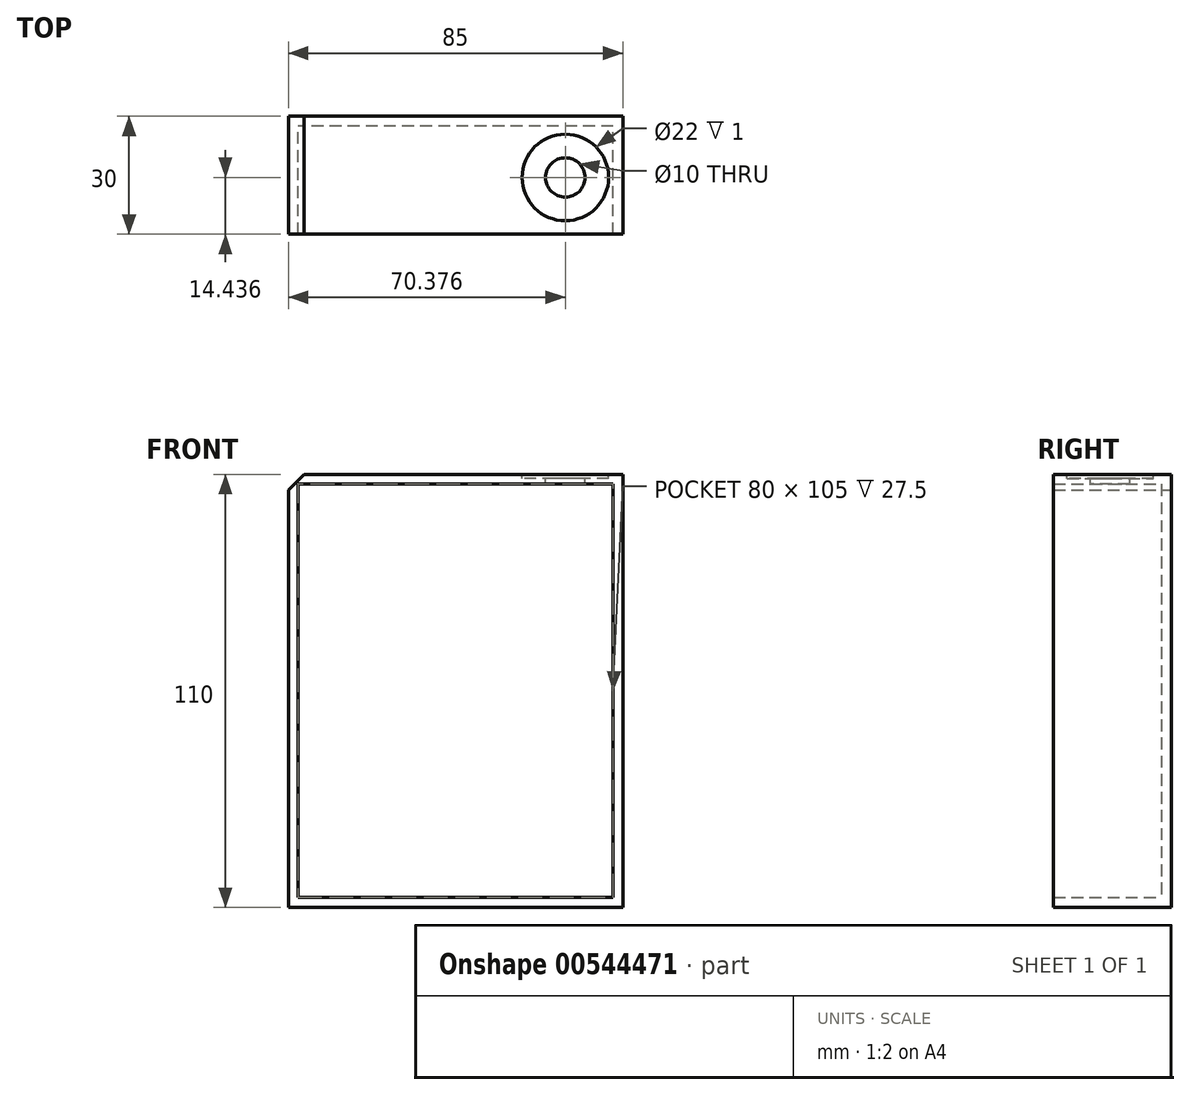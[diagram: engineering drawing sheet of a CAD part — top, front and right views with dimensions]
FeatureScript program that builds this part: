
annotation { "Feature Type Name" : "Feature", "Feature Type Description" : "" }
export const myFeature = defineFeature(function(context is Context, id is Id, definition is map)
    precondition{}
    {
        {
            var Q0;
            Q0=qCreatedBy(makeId("Front.planeOp"),FACE);
            var sketch = newSketch(context, id + "F0", { "sketchPlane" : qUnion([Q0])});
            skLineSegment(sketch, "E0.bottom", {"start": v(42.5, 55) * mm, "end": v(-42.5, 55) * mm});
            skLineSegment(sketch, "E0.top", {"start": v(42.5, -55) * mm, "end": v(-42.5, -55) * mm});
            skLineSegment(sketch, "E0.left", {"start": v(42.5, 55) * mm, "end": v(42.5, -55) * mm});
            skLineSegment(sketch, "E0.right", {"start": v(-42.5, 55) * mm, "end": v(-42.5, -55) * mm});
            skPoint(sketch, "E0.middle", {"position": v(0, 0) * mm});
            skLineSegment(sketch, "E1", {"start": v(-42.5, 37.63) * mm, "end": v(-24.86, 55) * mm});
            skSolve(sketch);
        }
        {
            var Q0;
            Q0 = qSketchRegion(id + "F0", true);
            extrude(context, id + "F1", {"entities" : qUnion([Q0]), "depth" : 30 * mm, "offsetDistance" : 25 * mm});
        }
        {
            var Q0;
            Q0=makeQuery(id+"F1.opExtrude","SWEPT_FACE",FACE,{"disambiguationData":[OSD([sQuery(id+"F0.wireOp",EDGE,"E0.bottom")])]});
            var sketch = newSketch(context, id + "F2", { "sketchPlane" : qUnion([Q0])});
            skCircle(sketch, "E2", {"center": v(25.32, -14.4) * mm, "radius": 11 * mm});
            skSolve(sketch);
        }
        {
            var Q0;
            Q0=makeQuery(id+"F2.imprint","IMPRINT",FACE,{"disambiguationData":[TD([[makeQuery(id+"F2.imprint","IMPRINT",EDGE,{"derivedFrom":sQuery(id+"F2.wireOp",EDGE,"E2")}),1.0]])]});
            extrude(context, id + "F3", {"entities" : qUnion([Q0]), "operationType" : NewBodyOperationType.ADD, "depth" : -0.5 * mm, "offsetDistance" : 25 * mm});
        }
        {
            var Q0;
            Q0=makeQuery(id+"F1.opExtrude","CAP_FACE",FACE,{"disambiguationData":[OSD([sQuery(id+"F0.wireOp",EDGE,"E0.bottom"),sQuery(id+"F0.wireOp",EDGE,"E0.top"),sQuery(id+"F0.wireOp",EDGE,"E0.left"),sQuery(id+"F0.wireOp",EDGE,"E0.right")])],"isStart":false});
            shell(context, id + "F4", {"entities" : qUnion([Q0]), "thickness" : 2.5 * mm});
        }
        {
            var Q0;
            Q0=makeQuery(id+"F1.opExtrude","SWEPT_FACE",FACE,{"disambiguationData":[OSD([sQuery(id+"F0.wireOp",EDGE,"E0.bottom")])]});
            var sketch = newSketch(context, id + "F5", { "sketchPlane" : qUnion([Q0])});
            skCircle(sketch, "E3", {"center": v(27.88, -15.56) * mm, "radius": 11 * mm});
            skSolve(sketch);
        }
        {
            var Q0;
            Q0 = qSketchRegion(id + "F5", true);
            extrude(context, id + "F6", {"entities" : qUnion([Q0]), "operationType" : NewBodyOperationType.REMOVE, "oppositeDirection" : true, "depth" : 1 * mm, "offsetDistance" : 25 * mm});
        }
        {
            var Q0;
            Q0=makeQuery(id+"F6.boolean.opBoolean","COPY",FACE,{"derivedFrom":makeQuery(id+"F6.opExtrude","CAP_FACE",FACE,{"disambiguationData":[OSD([sQuery(id+"F5.wireOp",EDGE,"E3")])],"isStart":false})});
            var sketch = newSketch(context, id + "F7", { "sketchPlane" : qUnion([Q0])});
            skCircle(sketch, "E4", {"center": v(27.88, -15.56) * mm, "radius": 5 * mm});
            skSolve(sketch);
        }
        {
            var Q0;
            Q0 = qSketchRegion(id + "F7", true);
            extrude(context, id + "F8", {"entities" : qUnion([Q0]), "operationType" : NewBodyOperationType.REMOVE, "oppositeDirection" : true, "depth" : 1.5 * mm, "offsetDistance" : 25 * mm});
        }
        {
            var Q0;
            Q0=makeQuery(id+"F1.opExtrude","SWEPT_EDGE",EDGE,{"disambiguationData":[OSD([sQuery(id+"F0.wireOp",EDGE,"E0.bottom"),sQuery(id+"F0.wireOp",EDGE,"E0.right")])]});
            chamfer(context, id + "F9", {"entities" : qUnion([Q0]), "chamferType" : ChamferType.OFFSET_ANGLE, "width" : 4 * mm, "oppositeDirection" : false, "angle" : 45 * degree, "tangentPropagation" : true});
        }
    });
